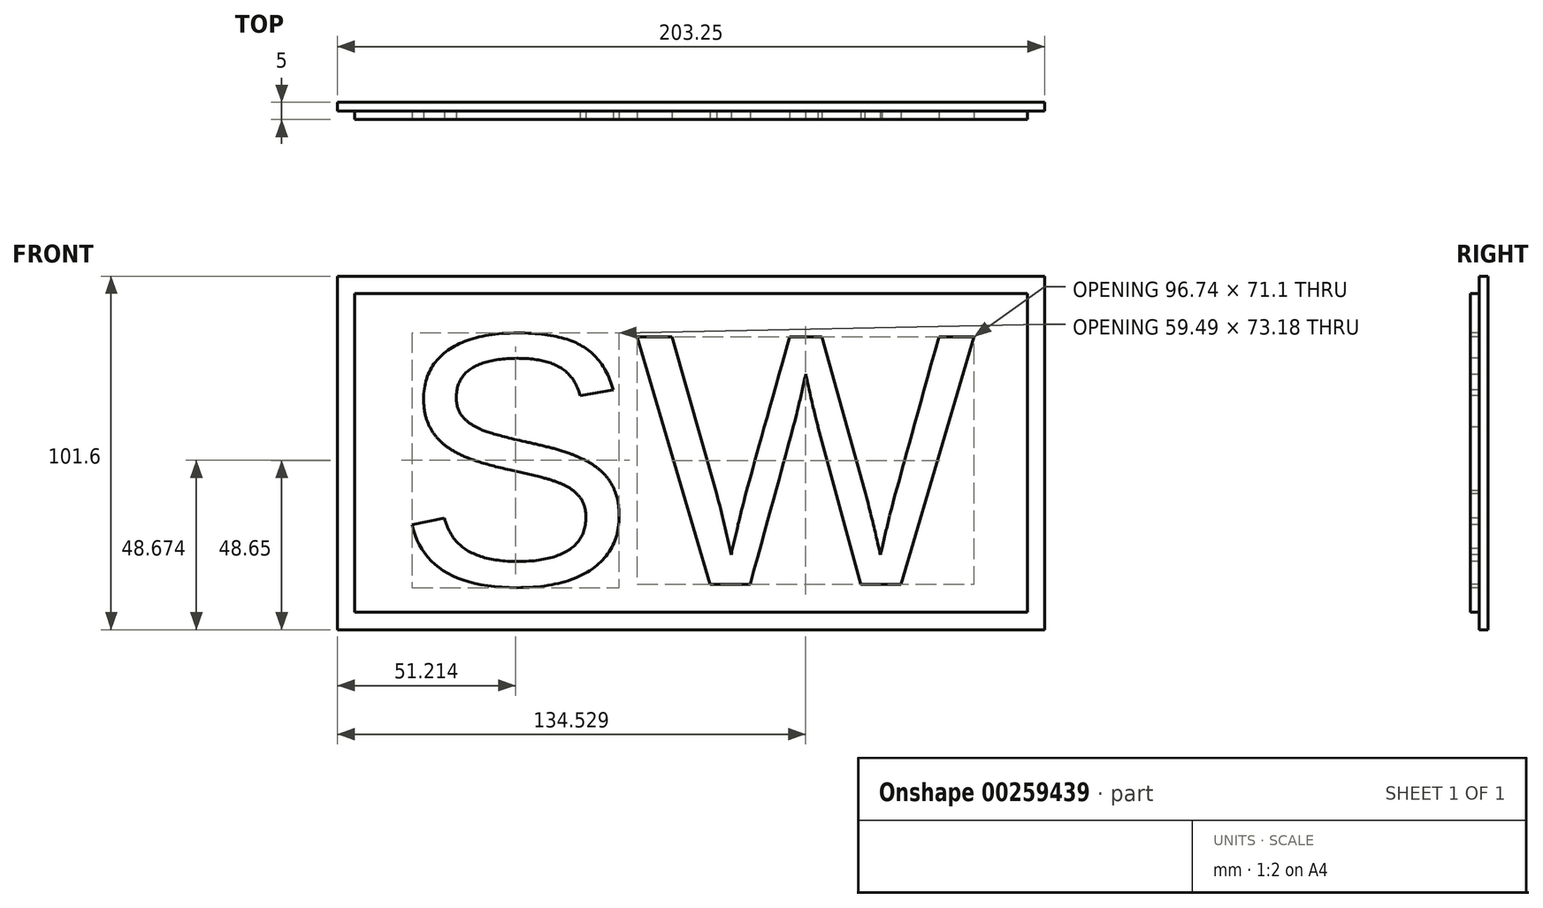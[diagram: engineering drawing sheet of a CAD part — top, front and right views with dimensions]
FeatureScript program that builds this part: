
annotation { "Feature Type Name" : "Feature", "Feature Type Description" : "" }
export const myFeature = defineFeature(function(context is Context, id is Id, definition is map)
    precondition{}
    {
        {
            var Q0;
            Q0=qCreatedBy(makeId("Front.planeOp"),FACE);
            var sketch = newSketch(context, id + "F0", { "sketchPlane" : qUnion([Q0])});
            skLineSegment(sketch, "E0.bottom", {"start": v(0, 0) * mm, "end": v(203.25, 0) * mm});
            skLineSegment(sketch, "E0.top", {"start": v(0, 101.6) * mm, "end": v(203.25, 101.6) * mm});
            skLineSegment(sketch, "E0.left", {"start": v(0, 0) * mm, "end": v(0, 101.6) * mm});
            skLineSegment(sketch, "E0.right", {"start": v(203.25, 0) * mm, "end": v(203.25, 101.6) * mm});
            skLineSegment(sketch, "E1.0", {"start": v(5, 5) * mm, "end": v(5, 96.6) * mm});
            skLineSegment(sketch, "E1.1", {"start": v(5, 5) * mm, "end": v(198.25, 5) * mm});
            skLineSegment(sketch, "E1.2", {"start": v(198.25, 5) * mm, "end": v(198.25, 96.6) * mm});
            skLineSegment(sketch, "E1.3", {"start": v(5, 96.6) * mm, "end": v(198.25, 96.6) * mm});
            skSolve(sketch);
        }
        {
            var Q0;
            Q0=makeQuery(id+"F0.imprint","IMPRINT",FACE,{"disambiguationData":[TD([[makeQuery(id+"F0.imprint","IMPRINT",EDGE,{"derivedFrom":sQuery(id+"F0.wireOp",EDGE,"E1.0")}),-1.0]])]});
            var Q1;
            Q1=makeQuery(id+"F0.imprint","IMPRINT",FACE,{"disambiguationData":[TD([[makeQuery(id+"F0.imprint","IMPRINT",EDGE,{"derivedFrom":sQuery(id+"F0.wireOp",EDGE,"E0.bottom")}),1.0]])]});
            extrude(context, id + "F1", {"entities" : qUnion([Q0, Q1]), "oppositeDirection" : true, "depth" : 2.5 * mm, "offsetDistance" : 25 * mm});
        }
        {
            var Q0;
            Q0=makeQuery(id+"F0.imprint","IMPRINT",FACE,{"disambiguationData":[TD([[makeQuery(id+"F0.imprint","IMPRINT",EDGE,{"derivedFrom":sQuery(id+"F0.wireOp",EDGE,"E1.0")}),-1.0]])]});
            extrude(context, id + "F2", {"entities" : qUnion([Q0]), "depth" : 2.5 * mm, "offsetDistance" : 25 * mm});
        }
        {
            var Q0;
            Q0=makeQuery(id+"F2.opExtrude","CAP_FACE",FACE,{"disambiguationData":[OSD([sQuery(id+"F0.wireOp",EDGE,"E1.0"),sQuery(id+"F0.wireOp",EDGE,"E1.1"),sQuery(id+"F0.wireOp",EDGE,"E1.2"),sQuery(id+"F0.wireOp",EDGE,"E1.3")])],"isStart":false});
            var sketch = newSketch(context, id + "F3", { "sketchPlane" : qUnion([Q0])});
            skLineSegment(sketch, "E2", {"start": v(5, 13.1) * mm, "end": v(198.25, 13.1) * mm, "construction": true});
            skText(sketch, "E3", { "text": "SW", "fontName": "Arimo-Regular.ttf"});
            const initialGuessF3  = {"E3": [0.01677, 0.0131, 1, 0, 0.07441]};
            skSetInitialGuess(sketch, initialGuessF3);
            skSolve(sketch);
        }
        {
            var Q0;
            Q0 = qSketchRegion(id + "F3", true);
            extrude(context, id + "F4", {"entities" : qUnion([Q0]), "operationType" : NewBodyOperationType.REMOVE, "oppositeDirection" : true, "depth" : 2.6 * mm, "offsetDistance" : 25 * mm});
        }
    });
